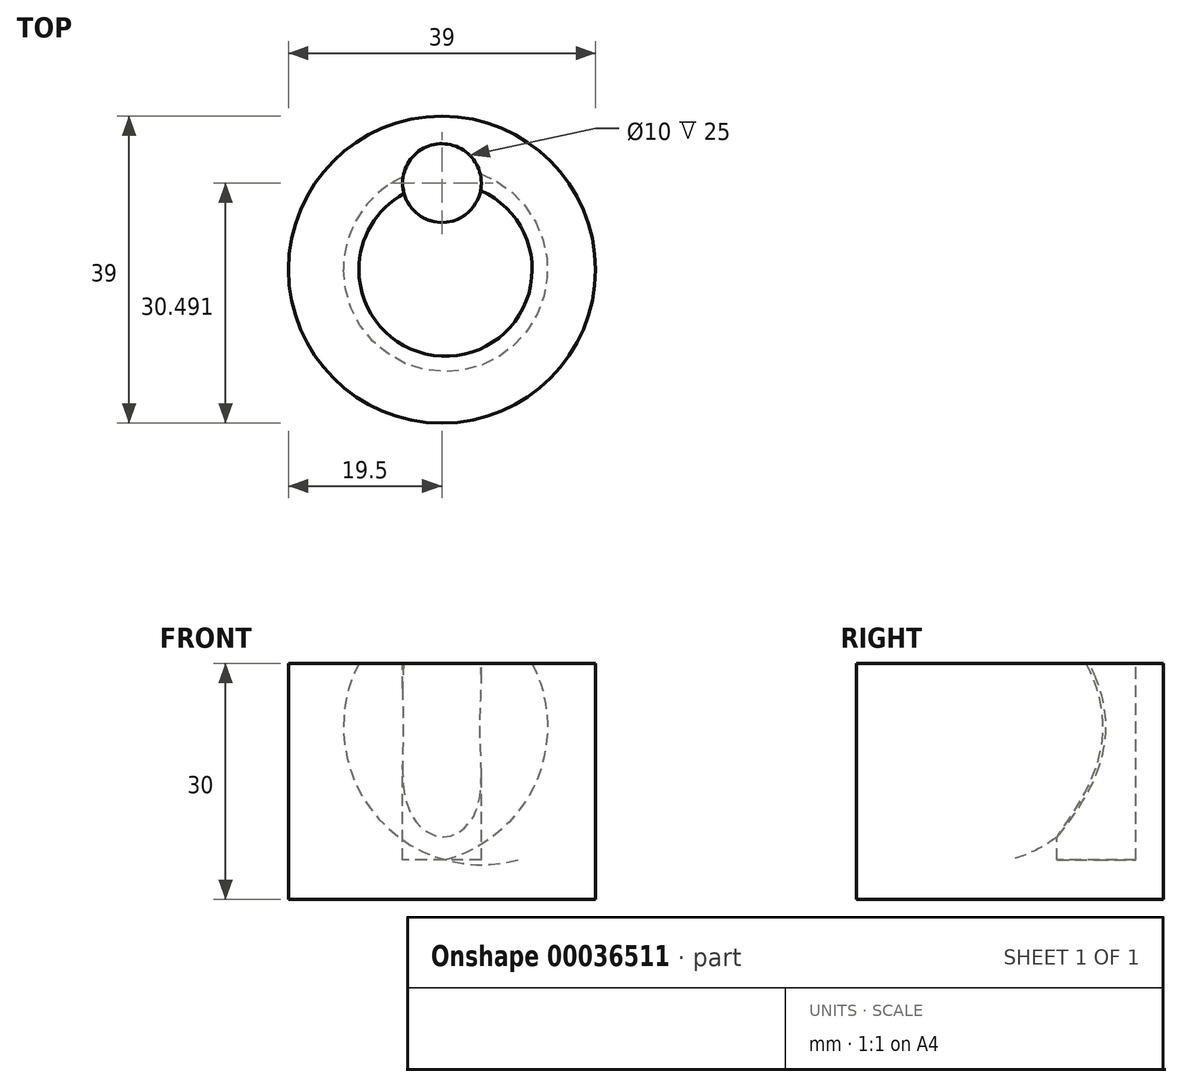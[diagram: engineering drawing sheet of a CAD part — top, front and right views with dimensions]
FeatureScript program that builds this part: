
annotation { "Feature Type Name" : "Feature", "Feature Type Description" : "" }
export const myFeature = defineFeature(function(context is Context, id is Id, definition is map)
    precondition{}
    {
        {
            var Q0;
            Q0=qCreatedBy(makeId("Top.planeOp"),FACE);
            var sketch = newSketch(context, id + "F0", { "sketchPlane" : qUnion([Q0])});
            skCircle(sketch, "E0", {"center": v(0, 0) * mm, "radius": 19.5 * mm});
            skSolve(sketch);
        }
        {
            var Q0;
            Q0=makeQuery(id+"F0.imprint","IMPRINT",FACE,{"disambiguationData":[TD([[makeQuery(id+"F0.imprint","IMPRINT",EDGE,{"derivedFrom":sQuery(id+"F0.wireOp",EDGE,"E0")}),1.0]])]});
            extrude(context, id + "F1", {"entities" : qUnion([Q0]), "depth" : 30 * mm, "offsetDistance" : 25 * mm});
        }
        {
            var Q0;
            Q0=qCreatedBy(makeId("Front.planeOp"),FACE);
            var sketch = newSketch(context, id + "F2", { "sketchPlane" : qUnion([Q0])});
            skLineSegment(sketch, "E1", {"start": v(0.45, 30) * mm, "end": v(11.45, 30) * mm});
            skLineSegment(sketch, "E2", {"start": v(11.45, 30) * mm, "end": v(0.45, 30) * mm});
            skLineSegment(sketch, "E3", {"start": v(0.45, 5) * mm, "end": v(0.45, 30) * mm});
            skArc(sketch, "E4", {"start": v(0.45, 5) * mm, "mid": v(11.93, 14.87) * mm, "end": v(11.45, 30) * mm});
            skSolve(sketch);
        }
        {
            var Q0;
            Q0 = qSketchRegion(id + "F2", true);
            var Q1;
            Q1=sQuery(id+"F2.wireOp",EDGE,"E3");
            revolve(context, id + "F3", {"operationType" : NewBodyOperationType.REMOVE, "surfaceOperationType" : NewSurfaceOperationType.NEW, "entities" : qUnion([Q0]), "axis" : qUnion([Q1]), "revolveType" : RevolveType.FULL, "oppositeDirection" : true});
        }
        {
            var Q0;
            Q0=makeQuery(id+"F1.opExtrude","CAP_FACE",FACE,{"disambiguationData":[OSD([sQuery(id+"F0.wireOp",EDGE,"E0")])],"isStart":false});
            var sketch = newSketch(context, id + "F4", { "sketchPlane" : qUnion([Q0])});
            skCircle(sketch, "E5", {"center": v(0, 11) * mm, "radius": 5 * mm});
            skSolve(sketch);
        }
        {
            var Q0;
            Q0 = qSketchRegion(id + "F4", true);
            extrude(context, id + "F5", {"entities" : qUnion([Q0]), "operationType" : NewBodyOperationType.REMOVE, "oppositeDirection" : true, "depth" : 25 * mm, "offsetDistance" : 25 * mm});
        }
    });
